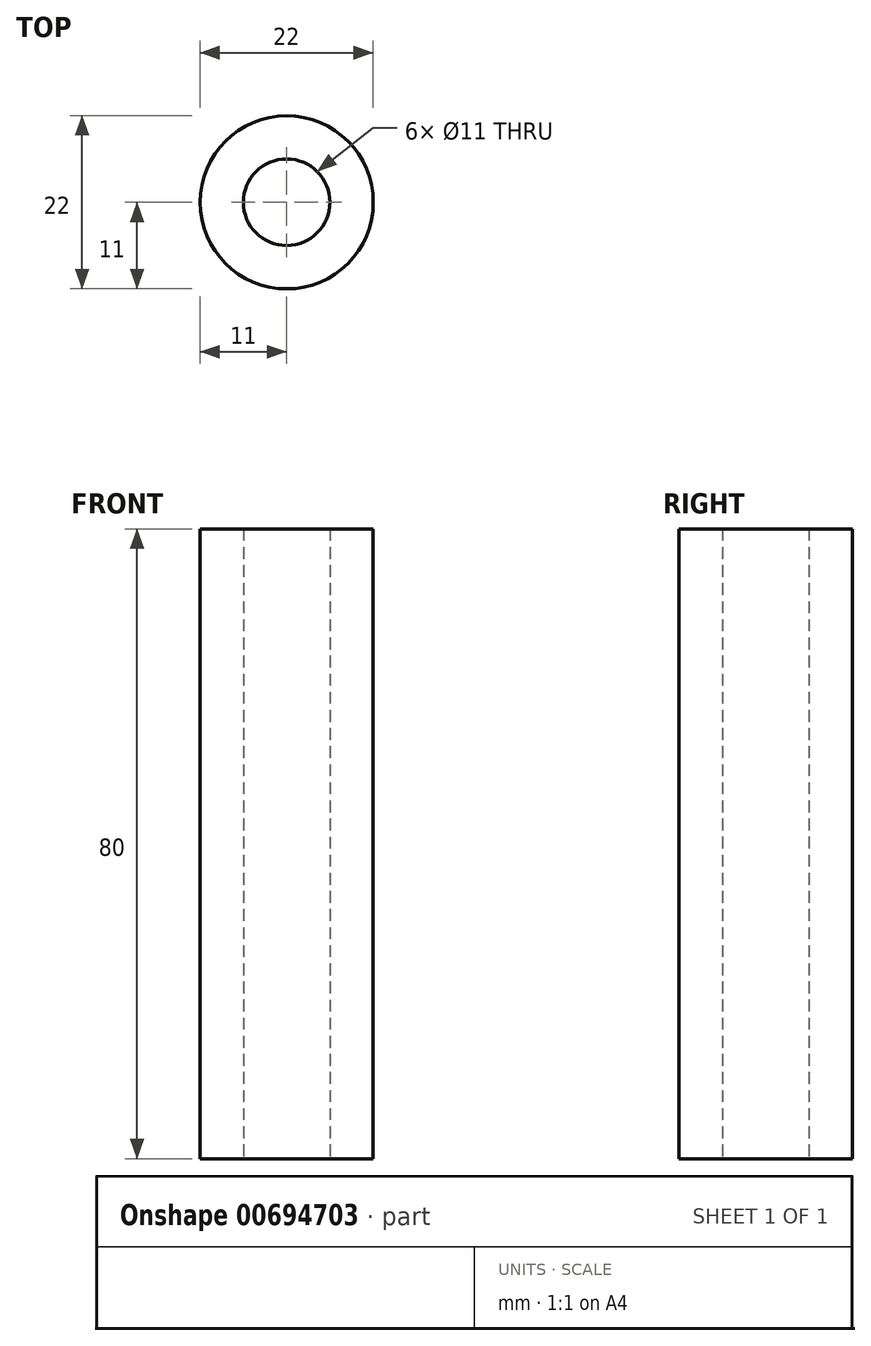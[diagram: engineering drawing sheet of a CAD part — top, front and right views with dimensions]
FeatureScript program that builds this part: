
annotation { "Feature Type Name" : "Feature", "Feature Type Description" : "" }
export const myFeature = defineFeature(function(context is Context, id is Id, definition is map)
    precondition{}
    {
        {
            var Q0;
            Q0=qCreatedBy(makeId("Top.planeOp"),FACE);
            var sketch = newSketch(context, id + "F0", { "sketchPlane" : qUnion([Q0])});
            skCircle(sketch, "E0", {"center": v(0, 0) * mm, "radius": 11 * mm});
            skCircle(sketch, "E1", {"center": v(0, 0) * mm, "radius": 5.5 * mm});
            skSolve(sketch);
        }
        {
            var Q0;
            Q0=makeQuery(id+"F0.imprint","IMPRINT",FACE,{"disambiguationData":[TD([[makeQuery(id+"F0.imprint","IMPRINT",EDGE,{"derivedFrom":sQuery(id+"F0.wireOp",EDGE,"E0")}),1.0]])]});
            extrude(context, id + "F1", {"entities" : qUnion([Q0]), "depth" : 80 * mm, "offsetDistance" : 25 * mm});
        }
    });
